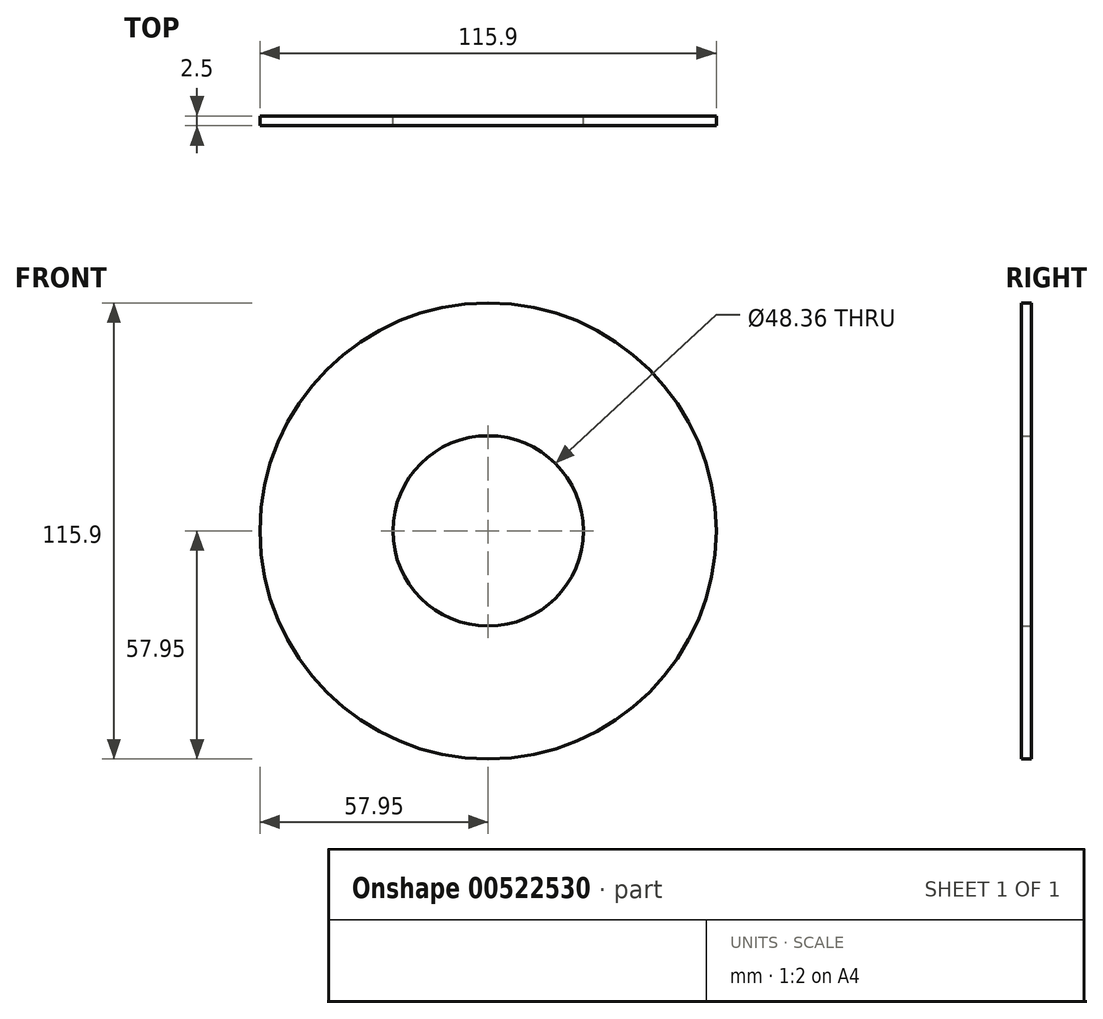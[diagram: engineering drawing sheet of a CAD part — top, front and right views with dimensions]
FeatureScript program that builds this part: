
annotation { "Feature Type Name" : "Feature", "Feature Type Description" : "" }
export const myFeature = defineFeature(function(context is Context, id is Id, definition is map)
    precondition{}
    {
        {
            var Q0;
            Q0=qCreatedBy(makeId("Front.planeOp"),FACE);
            var sketch = newSketch(context, id + "F0", { "sketchPlane" : qUnion([Q0])});
            skCircle(sketch, "E0", {"center": v(0, 0) * mm, "radius": 57.95 * mm});
            skCircle(sketch, "E1", {"center": v(0, 0) * mm, "radius": 24.18 * mm});
            skSolve(sketch);
        }
        {
            var Q0;
            Q0=makeQuery(id+"F0.imprint","IMPRINT",FACE,{"disambiguationData":[TD([[makeQuery(id+"F0.imprint","IMPRINT",EDGE,{"derivedFrom":sQuery(id+"F0.wireOp",EDGE,"E0")}),1.0]])]});
            extrude(context, id + "F1", {"entities" : qUnion([Q0]), "depth" : 2.5 * mm, "offsetDistance" : 25.4 * mm});
        }
    });
